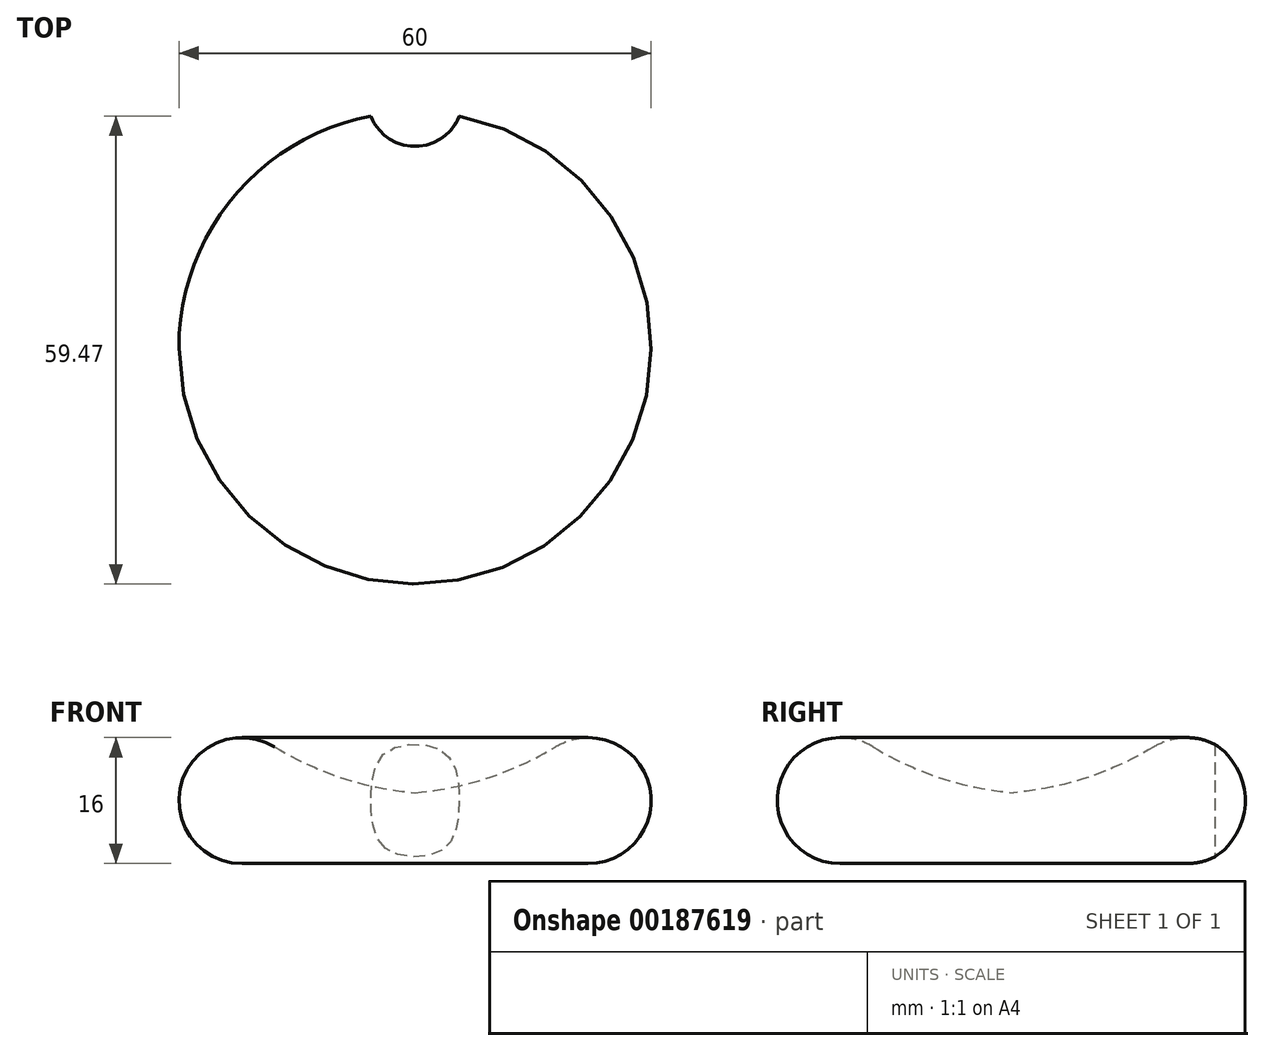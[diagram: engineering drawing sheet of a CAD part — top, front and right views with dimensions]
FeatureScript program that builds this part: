
annotation { "Feature Type Name" : "Feature", "Feature Type Description" : "" }
export const myFeature = defineFeature(function(context is Context, id is Id, definition is map)
    precondition{}
    {
        {
            var Q0;
            Q0=qCreatedBy(makeId("Front.planeOp"),FACE);
            var sketch = newSketch(context, id + "F0", { "sketchPlane" : qUnion([Q0])});
            skArc(sketch, "E0", {"start": v(-17.83, 14.83) * mm, "mid": v(-29.7, 10.17) * mm, "end": v(-22, 0) * mm});
            skLineSegment(sketch, "E1", {"start": v(0, 0) * mm, "end": v(0, 9) * mm});
            skLineSegment(sketch, "E2", {"start": v(0, 0) * mm, "end": v(-22, 0) * mm});
            skArc(sketch, "E3", {"start": v(-17.83, 14.83) * mm, "mid": v(-9.26, 10.87) * mm, "end": v(0, 9) * mm});
            skSolve(sketch);
        }
        {
            var Q0;
            Q0 = qSketchRegion(id + "F0", true);
            var Q1;
            Q1=sQuery(id+"F0.wireOp",EDGE,"E1");
            revolve(context, id + "F1", {"entities" : qUnion([Q0]), "axis" : qUnion([Q1]), "revolveType" : RevolveType.FULL});
        }
        {
            var Q0;
            Q0=qCreatedBy(makeId("Top.planeOp"),FACE);
            var sketch = newSketch(context, id + "F2", { "sketchPlane" : qUnion([Q0])});
            skCircle(sketch, "E4", {"center": v(0, 31.6) * mm, "radius": 6 * mm});
            skSolve(sketch);
        }
        {
            var Q0;
            Q0=makeQuery(id+"F2.imprint","IMPRINT",FACE,{"disambiguationData":[TD([[makeQuery(id+"F2.imprint","IMPRINT",EDGE,{"derivedFrom":sQuery(id+"F2.wireOp",EDGE,"E4")}),1.0]])]});
            extrude(context, id + "F3", {"entities" : qUnion([Q0]), "operationType" : NewBodyOperationType.REMOVE, "endBound" : BoundingType.THROUGH_ALL, "depth" : 25 * mm});
        }
        {
            var Q0;
            Q0=qCreatedBy(makeId("Top.planeOp"),FACE);
            cPlane(context, id + "F4", {"entities" : qUnion([Q0]), "cplaneType" : CPlaneType.OFFSET, "offset" : 18 * mm, "width" : 150 * mm, "height" : 150 * mm});
        }
    });
